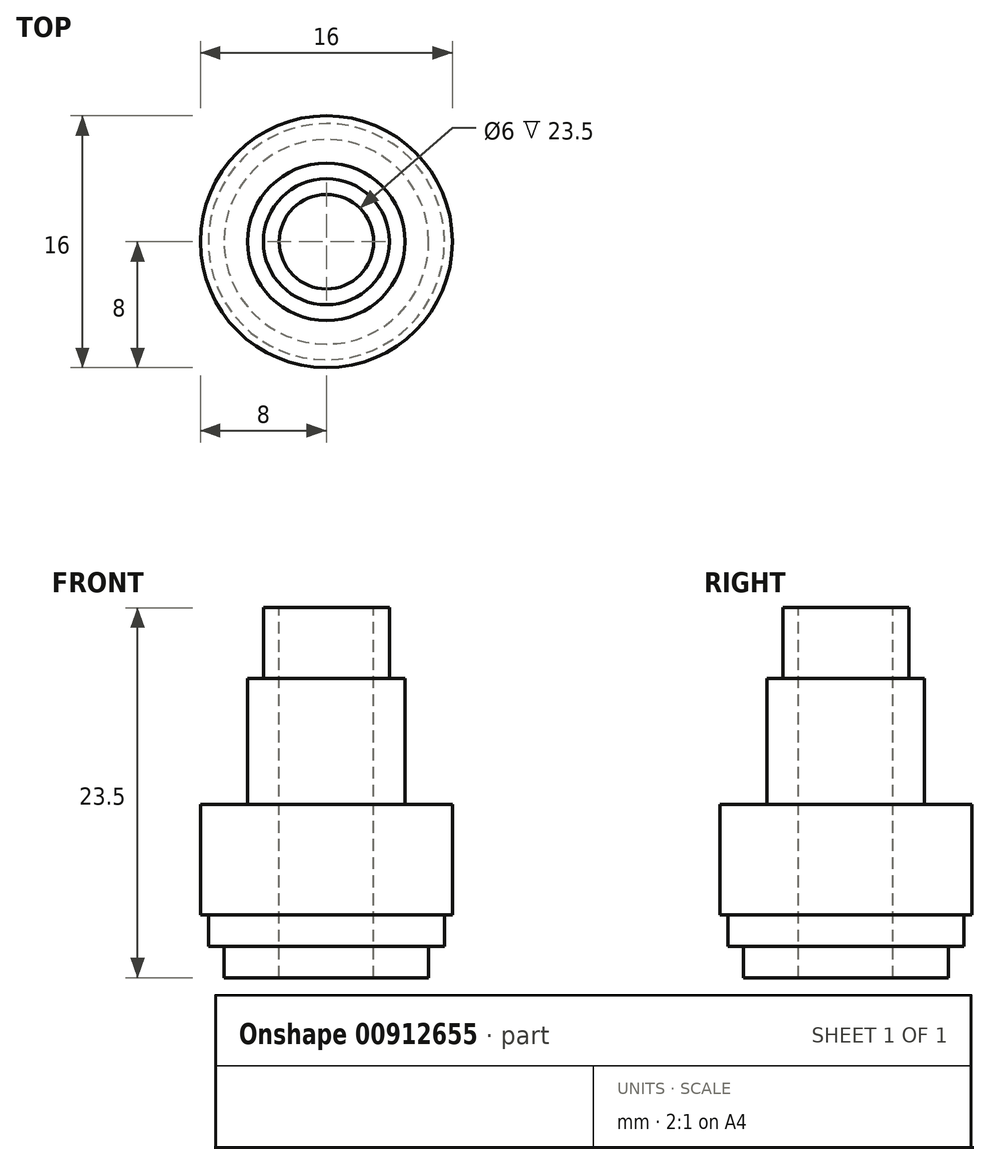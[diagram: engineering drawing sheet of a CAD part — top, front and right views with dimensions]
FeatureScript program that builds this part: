
annotation { "Feature Type Name" : "Feature", "Feature Type Description" : "" }
export const myFeature = defineFeature(function(context is Context, id is Id, definition is map)
    precondition{}
    {
        {
            var Q0;
            Q0=qCreatedBy(makeId("Front.planeOp"),FACE);
            var sketch = newSketch(context, id + "F0", { "sketchPlane" : qUnion([Q0])});
            skLineSegment(sketch, "E0", {"start": v(3, 9.87) * mm, "end": v(3, -13.63) * mm});
            skLineSegment(sketch, "E1", {"start": v(3, -13.63) * mm, "end": v(6.5, -13.63) * mm});
            skLineSegment(sketch, "E2", {"start": v(6.5, -13.63) * mm, "end": v(6.5, -11.63) * mm});
            skLineSegment(sketch, "E3", {"start": v(6.5, -11.63) * mm, "end": v(7.5, -11.63) * mm});
            skLineSegment(sketch, "E4", {"start": v(7.5, -11.63) * mm, "end": v(7.5, -9.63) * mm});
            skLineSegment(sketch, "E5", {"start": v(7.5, -9.63) * mm, "end": v(8, -9.63) * mm});
            skLineSegment(sketch, "E6", {"start": v(8, -9.63) * mm, "end": v(8, -2.63) * mm});
            skLineSegment(sketch, "E7", {"start": v(8, -2.63) * mm, "end": v(5, -2.63) * mm});
            skLineSegment(sketch, "E8", {"start": v(5, -2.63) * mm, "end": v(5, 5.37) * mm});
            skLineSegment(sketch, "E9", {"start": v(5, 5.37) * mm, "end": v(4, 5.37) * mm});
            skLineSegment(sketch, "E10", {"start": v(4, 5.37) * mm, "end": v(4, 9.87) * mm});
            skLineSegment(sketch, "E11", {"start": v(4, 9.87) * mm, "end": v(3, 9.87) * mm});
            skLineSegment(sketch, "E12", {"start": v(0, 23.64) * mm, "end": v(0, 19.05) * mm, "construction": true});
            skSolve(sketch);
        }
        {
            var Q0;
            Q0=makeQuery(id+"F0.imprint","IMPRINT",FACE,{"disambiguationData":[TD([[makeQuery(id+"F0.imprint","IMPRINT",EDGE,{"derivedFrom":sQuery(id+"F0.wireOp",EDGE,"E0")}),1.0]])]});
            var Q1;
            Q1=sQuery(id+"F0.wireOp",EDGE,"E12");
            revolve(context, id + "F1", {"surfaceOperationType" : NewSurfaceOperationType.NEW, "entities" : qUnion([Q0]), "axis" : qUnion([Q1]), "revolveType" : RevolveType.FULL});
        }
    });
